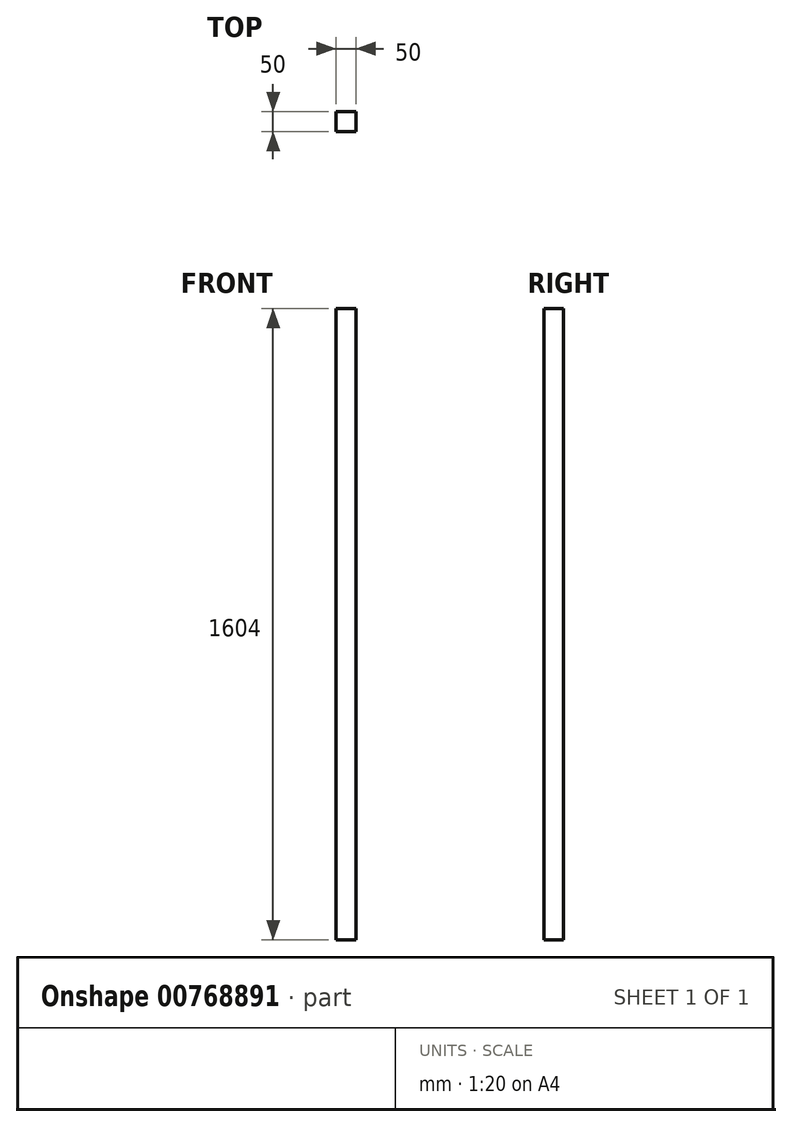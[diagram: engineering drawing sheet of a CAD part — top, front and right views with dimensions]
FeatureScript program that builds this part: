
annotation { "Feature Type Name" : "Feature", "Feature Type Description" : "" }
export const myFeature = defineFeature(function(context is Context, id is Id, definition is map)
    precondition{}
    {
        {
            var Q0;
            Q0=qCreatedBy(makeId("Front.planeOp"),FACE);
            var sketch = newSketch(context, id + "F0", { "sketchPlane" : qUnion([Q0])});
            skLineSegment(sketch, "E0.bottom", {"start": v(0, 0) * mm, "end": v(50, 0) * mm});
            skLineSegment(sketch, "E0.top", {"start": v(0, 1604) * mm, "end": v(50, 1604) * mm});
            skLineSegment(sketch, "E0.left", {"start": v(0, 0) * mm, "end": v(0, 1604) * mm});
            skLineSegment(sketch, "E0.right", {"start": v(50, 0) * mm, "end": v(50, 1604) * mm});
            skSolve(sketch);
        }
        {
            var Q0;
            Q0=makeQuery(id+"F0.imprint","IMPRINT",FACE,{"disambiguationData":[TD([[makeQuery(id+"F0.imprint","IMPRINT",EDGE,{"derivedFrom":sQuery(id+"F0.wireOp",EDGE,"E0.bottom")}),1.0]])]});
            extrude(context, id + "F1", {"entities" : qUnion([Q0]), "depth" : 50 * mm, "offsetDistance" : 25 * mm});
        }
    });
